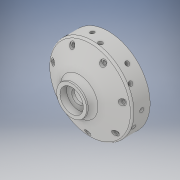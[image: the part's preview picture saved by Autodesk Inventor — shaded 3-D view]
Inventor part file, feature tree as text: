
AUTODESK INVENTOR PART (.ipt)
format: ipt  version: 2018 (Build 220112000, 112)  size: 351,744 bytes
history: native  units: mm
features: sketch x4, revolve x2, extrude x1, hole x1, other x1, pattern_circular x1
ambient origin geometry x8: Origin, YZ Plane, XZ Plane, XY Plane, X Axis, Y Axis, Z Axis, Center Point
bodies: Solid1 (feature_tree)
feature tree (10):
  revolve  "Revolution1"  [1 undecoded]
  extrude  "Extrusion1"  Depth=4.0mm
  hole  "Hole1"  [1 undecoded]
  revolve  "Revolution2"  [1 undecoded]
  other  "Work Axis1"
  pattern_circular  "Circular Pattern1"  [2 undecoded]
  sketch  "Sketch1"  dims[d0=50.0mm d1=45.0mm]
  sketch  "Sketch2"  dims[d2=40.5mm d3=4.0mm]
  sketch  "Sketch3"  dims[d4=32.5mm d5=44.0mm]
  sketch  "Sketch4"  dims[d6=3.5mm d7=18.0mm d8=14.0mm d9=4.63734mm d10=8.0mm d11=3.5mm d12=8.0mm d13=3.0mm d14=90.0deg d15=5.0mm d16=7.0mm d17=9.21mm d18=10.0mm d19=16.5mm d20=59.5mm d21=0.0mm d22=2.25mm d23=4.0mm d24=6.0mm d25=4.0mm d26=2.0mm d27=90.0deg d28=24.5mm d29=0.0mm d30=3.5mm d31=19.0mm d32=5.0mm d33=90.0deg d34=70.0mm d35=360.0deg]
note: 5 required parameter values undecoded (feature->parameter linkage not recoverable at this tier; creation-order binding heuristic only, values carry confidence <= 0.55)